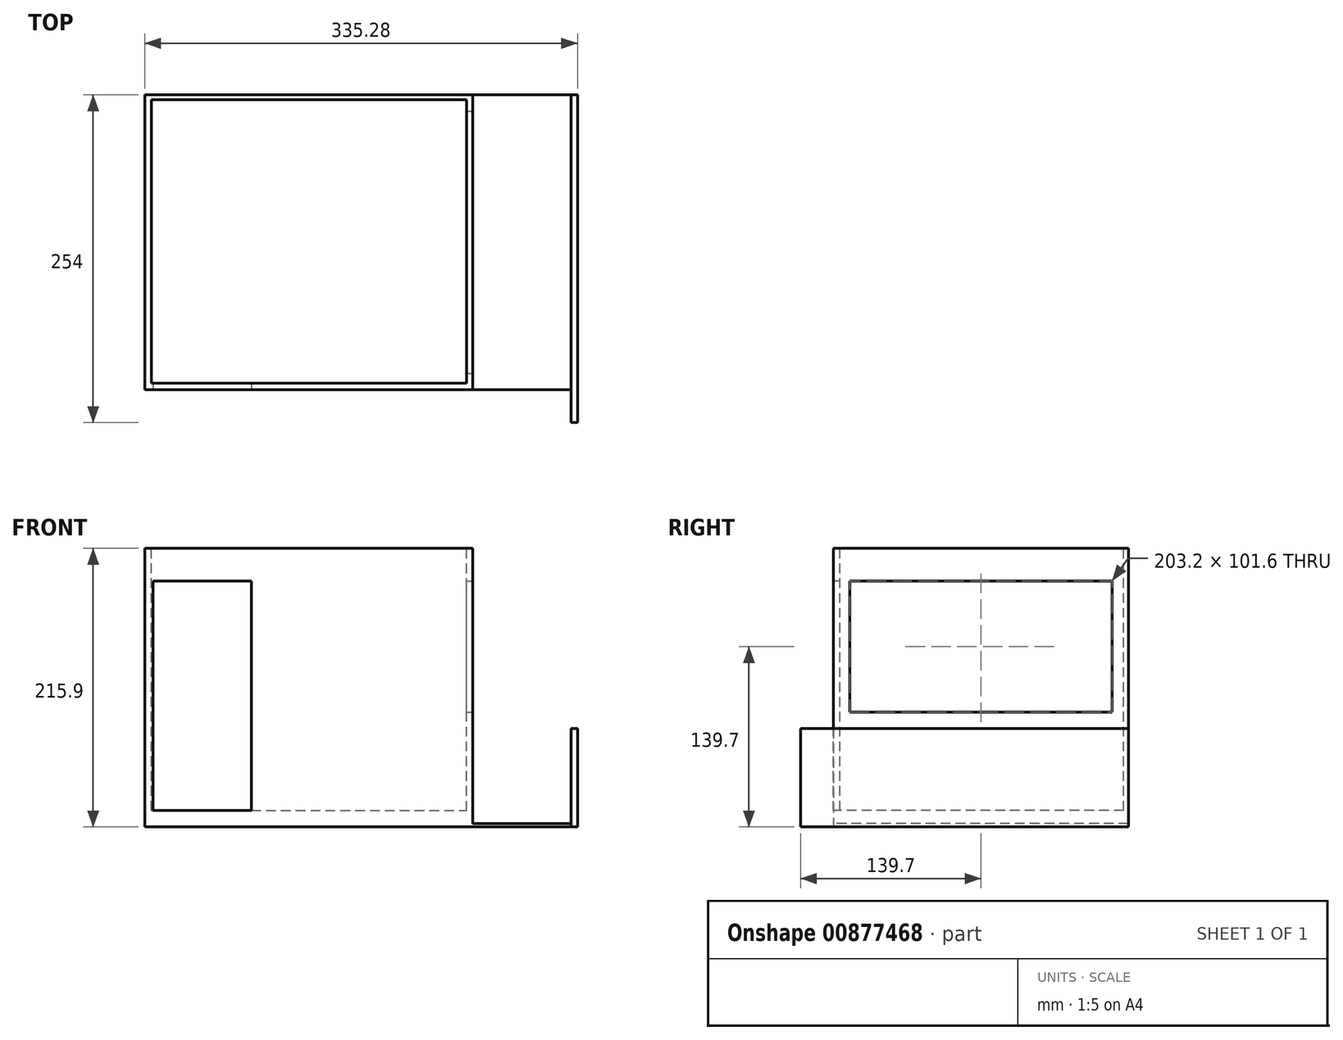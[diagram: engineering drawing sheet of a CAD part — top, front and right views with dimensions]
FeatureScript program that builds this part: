
annotation { "Feature Type Name" : "Feature", "Feature Type Description" : "" }
export const myFeature = defineFeature(function(context is Context, id is Id, definition is map)
    precondition{}
    {
        {
            var Q0;
            Q0=qCreatedBy(makeId("Top.planeOp"),FACE);
            var sketch = newSketch(context, id + "F0", { "sketchPlane" : qUnion([Q0])});
            skLineSegment(sketch, "E0.bottom", {"start": v(81.28, 76.2) * mm, "end": v(76.2, 76.2) * mm});
            skLineSegment(sketch, "E0.top", {"start": v(81.28, -177.8) * mm, "end": v(76.2, -177.8) * mm});
            skLineSegment(sketch, "E0.left", {"start": v(81.28, 76.2) * mm, "end": v(81.28, -177.8) * mm});
            skLineSegment(sketch, "E0.right", {"start": v(76.2, 76.2) * mm, "end": v(76.2, -177.8) * mm});
            skSolve(sketch);
        }
        {
            var Q0;
            Q0 = qSketchRegion(id + "F0", true);
            extrude(context, id + "F1", {"entities" : qUnion([Q0]), "depth" : 76.2 * mm, "offsetDistance" : 25.4 * mm});
        }
        {
            var Q0;
            Q0=qCreatedBy(makeId("Top.planeOp"),FACE);
            var sketch = newSketch(context, id + "F2", { "sketchPlane" : qUnion([Q0])});
            skLineSegment(sketch, "E1.bottom", {"start": v(76.2, 76.2) * mm, "end": v(0, 76.2) * mm});
            skLineSegment(sketch, "E1.top", {"start": v(76.2, -152.4) * mm, "end": v(0, -152.4) * mm});
            skLineSegment(sketch, "E1.left", {"start": v(76.2, 76.2) * mm, "end": v(76.2, -152.4) * mm});
            skLineSegment(sketch, "E1.right", {"start": v(0, 76.2) * mm, "end": v(0, -152.4) * mm});
            skSolve(sketch);
        }
        {
            var Q0;
            Q0 = qSketchRegion(id + "F2", true);
            extrude(context, id + "F3", {"entities" : qUnion([Q0]), "operationType" : NewBodyOperationType.ADD, "depth" : 2.54 * mm, "offsetDistance" : 25.4 * mm});
        }
        {
            var Q0;
            Q0=qCreatedBy(makeId("Top.planeOp"),FACE);
            var sketch = newSketch(context, id + "F4", { "sketchPlane" : qUnion([Q0])});
            skLineSegment(sketch, "E2.bottom", {"start": v(0, 76.2) * mm, "end": v(-254, 76.2) * mm});
            skLineSegment(sketch, "E2.top", {"start": v(0, -152.4) * mm, "end": v(-254, -152.4) * mm});
            skLineSegment(sketch, "E2.left", {"start": v(0, 76.2) * mm, "end": v(0, -152.4) * mm});
            skLineSegment(sketch, "E2.right", {"start": v(-254, 76.2) * mm, "end": v(-254, -152.4) * mm});
            skSolve(sketch);
        }
        {
            var Q0;
            Q0 = qSketchRegion(id + "F4", true);
            extrude(context, id + "F5", {"entities" : qUnion([Q0]), "operationType" : NewBodyOperationType.ADD, "depth" : 12.7 * mm, "offsetDistance" : 25.4 * mm});
        }
        {
            var Q0;
            Q0=makeQuery(id+"F5.opExtrude","CAP_FACE",FACE,{"disambiguationData":[OSD([sQuery(id+"F4.wireOp",EDGE,"E2.bottom"),sQuery(id+"F4.wireOp",EDGE,"E2.top"),sQuery(id+"F4.wireOp",EDGE,"E2.left"),sQuery(id+"F4.wireOp",EDGE,"E2.right")])],"isStart":false});
            var sketch = newSketch(context, id + "F6", { "sketchPlane" : qUnion([Q0])});
            skLineSegment(sketch, "E3.bottom", {"start": v(-254, 76.2) * mm, "end": v(0, 76.2) * mm});
            skLineSegment(sketch, "E3.top", {"start": v(-254, -152.4) * mm, "end": v(0, -152.4) * mm});
            skLineSegment(sketch, "E3.left", {"start": v(-254, 76.2) * mm, "end": v(-254, -152.4) * mm});
            skLineSegment(sketch, "E3.right", {"start": v(0, 76.2) * mm, "end": v(0, -152.4) * mm});
            skSolve(sketch);
        }
        {
            var Q0;
            Q0 = qSketchRegion(id + "F6", true);
            extrude(context, id + "F7", {"entities" : qUnion([Q0]), "operationType" : NewBodyOperationType.ADD, "depth" : 203.2 * mm, "offsetDistance" : 25.4 * mm});
        }
        {
            var Q0;
            Q0=makeQuery(id+"F7.opExtrude","CAP_FACE",FACE,{"disambiguationData":[OSD([sQuery(id+"F6.wireOp",EDGE,"E3.bottom"),sQuery(id+"F6.wireOp",EDGE,"E3.top"),sQuery(id+"F6.wireOp",EDGE,"E3.left"),sQuery(id+"F6.wireOp",EDGE,"E3.right")])],"isStart":false});
            var sketch = newSketch(context, id + "F8", { "sketchPlane" : qUnion([Q0])});
            skLineSegment(sketch, "E4.bottom", {"start": v(-248.92, 72.51) * mm, "end": v(-4.72, 72.51) * mm});
            skLineSegment(sketch, "E4.top", {"start": v(-248.92, -147.32) * mm, "end": v(-4.72, -147.32) * mm});
            skLineSegment(sketch, "E4.left", {"start": v(-248.92, 72.51) * mm, "end": v(-248.92, -147.32) * mm});
            skLineSegment(sketch, "E4.right", {"start": v(-4.72, 72.51) * mm, "end": v(-4.72, -147.32) * mm});
            skSolve(sketch);
        }
        {
            var Q0;
            Q0 = qSketchRegion(id + "F8", true);
            extrude(context, id + "F9", {"entities" : qUnion([Q0]), "operationType" : NewBodyOperationType.REMOVE, "oppositeDirection" : true, "depth" : 203.2 * mm, "offsetDistance" : 25.4 * mm});
        }
        {
            var Q0;
            Q0=makeQuery(id+"F7.boolean.opBoolean","MERGE",FACE,{"derivedFrom":[makeQuery(id+"F5.opExtrude","SWEPT_FACE",FACE,{"disambiguationData":[OSD([sQuery(id+"F4.wireOp",EDGE,"E2.left")])]}),makeQuery(id+"F7.opExtrude","SWEPT_FACE",FACE,{"disambiguationData":[OSD([sQuery(id+"F6.wireOp",EDGE,"E3.right")])]})]});
            var sketch = newSketch(context, id + "F10", { "sketchPlane" : qUnion([Q0])});
            skLineSegment(sketch, "E5.bottom", {"start": v(-139.7, 190.5) * mm, "end": v(63.5, 190.5) * mm});
            skLineSegment(sketch, "E5.top", {"start": v(-139.7, 88.9) * mm, "end": v(63.5, 88.9) * mm});
            skLineSegment(sketch, "E5.left", {"start": v(-139.7, 190.5) * mm, "end": v(-139.7, 88.9) * mm});
            skLineSegment(sketch, "E5.right", {"start": v(63.5, 190.5) * mm, "end": v(63.5, 88.9) * mm});
            skSolve(sketch);
        }
        {
            var Q0;
            Q0 = qSketchRegion(id + "F10", true);
            extrude(context, id + "F11", {"entities" : qUnion([Q0]), "operationType" : NewBodyOperationType.REMOVE, "oppositeDirection" : true, "depth" : 25.4 * mm, "offsetDistance" : 25.4 * mm});
        }
        {
            var Q0;
            Q0=makeQuery(id+"F7.boolean.opBoolean","MERGE",FACE,{"derivedFrom":[makeQuery(id+"F5.boolean.opBoolean","MERGE",FACE,{"derivedFrom":[makeQuery(id+"F3.opExtrude","SWEPT_FACE",FACE,{"disambiguationData":[OSD([sQuery(id+"F2.wireOp",EDGE,"E1.top")])]}),makeQuery(id+"F5.opExtrude","SWEPT_FACE",FACE,{"disambiguationData":[OSD([sQuery(id+"F4.wireOp",EDGE,"E2.top")])]})]}),makeQuery(id+"F7.opExtrude","SWEPT_FACE",FACE,{"disambiguationData":[OSD([sQuery(id+"F6.wireOp",EDGE,"E3.top")])]})]});
            var sketch = newSketch(context, id + "F12", { "sketchPlane" : qUnion([Q0])});
            skLineSegment(sketch, "E6.bottom", {"start": v(-247.65, 12.7) * mm, "end": v(-171.45, 12.7) * mm});
            skLineSegment(sketch, "E6.top", {"start": v(-247.65, 190.5) * mm, "end": v(-171.45, 190.5) * mm});
            skLineSegment(sketch, "E6.left", {"start": v(-247.65, 12.7) * mm, "end": v(-247.65, 190.5) * mm});
            skLineSegment(sketch, "E6.right", {"start": v(-171.45, 12.7) * mm, "end": v(-171.45, 190.5) * mm});
            skSolve(sketch);
        }
        {
            var Q0;
            Q0 = qSketchRegion(id + "F12", true);
            extrude(context, id + "F13", {"entities" : qUnion([Q0]), "operationType" : NewBodyOperationType.REMOVE, "oppositeDirection" : true, "depth" : 25.4 * mm, "offsetDistance" : 25.4 * mm});
        }
    });
